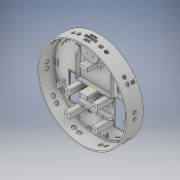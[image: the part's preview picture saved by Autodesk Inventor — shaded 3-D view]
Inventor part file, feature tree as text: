
AUTODESK INVENTOR PART (.ipt)
format: ipt  version: 2018 (Build 220112000, 112)  size: 3,257,856 bytes
history: native  units: in
note: dims shown in document units (in); Inventor stores cm internally (conversion verified against a paired STEP export)
features: extrude x34, fillet x14, sketch x12, chamfer x9, plane x3, emboss x3, pattern_circular x1
ambient origin geometry x8: Origin, YZ Plane, XZ Plane, XY Plane, X Axis, Y Axis, Z Axis, Center Point
bodies: Solid1 (feature_tree)
feature tree (76):
  sketch  "Sketch1"  dims[d0=15.748in d1=13.7795in]
  extrude  "Extrusion1"  Depth=13.7795in
  extrude  "Extrusion3"  Depth=1.9685in
  extrude  "Extrusion4"  Depth=1.9685in
  extrude  "Extrusion5"  Depth=7.874in
  extrude  "Extrusion6"  Depth=1.6811in
  extrude  "Extrusion8"  Depth=1.5748in
  extrude  "Extrusion9"  Depth=2.2835in
  chamfer  "Chamfer1"  Distance=0.4724in
  fillet  "Fillet2"  Radius=0.4724in
  fillet  "Fillet3"  Radius=2.0472in
  fillet  "Fillet4"  Radius=2.2638in
  extrude  "Extrusion12"  Depth=0.3937in
  extrude  "Extrusion15"  Depth=0.3937in
  extrude  "Extrusion16"  Depth=0.3937in
  extrude  "Extrusion17"  Depth=0.3937in
  chamfer  "Chamfer9"  Distance=0.7087in
  extrude  "Extrusion18"  Depth=0.3937in
  extrude  "Extrusion19"  Depth=0.3937in
  plane  "Work Plane1"
  extrude  "Extrusion20"  Depth=0.3937in
  fillet  "Fillet8"  Radius=1.9685in
  pattern_circular  "Circular Pattern1"  [2 undecoded]
  extrude  "Extrusion21"  Depth=0.3937in
  fillet  "Fillet9"  Radius=1.9685in
  sketch  "Sketch6"  dims[d12=3.7795in d13=1.6811in]
  sketch  "Sketch7"  dims[d14=2.3622in d15=1.5748in]
  sketch  "Sketch8"  dims[d16=1.5748in d27=2.2835in]
  extrude  "Extrusion22"  Depth=0.3937in
  extrude  "Extrusion23"  Depth=0.3937in
  extrude  "Extrusion24"  Depth=0.3937in
  extrude  "Extrusion25"  Depth=0.3937in
  fillet  "Fillet12"  Radius=0.3937in
  fillet  "Fillet14"  Radius=0.1181in
  extrude  "Extrusion26"  Depth=0.3937in
  extrude  "Extrusion27"  Depth=0.3937in
  extrude  "Extrusion28"  Depth=0.3937in
  extrude  "Extrusion29"  Depth=0.3937in
  extrude  "Extrusion30"  Depth=0.3937in
  extrude  "Extrusion31"  Depth=0.3937in
  extrude  "Extrusion32"  Depth=0.3937in
  extrude  "Extrusion33"  Depth=0.3937in
  extrude  "Extrusion34"  Depth=0.3937in
  extrude  "Extrusion35"  Depth=0.3937in
  emboss  "Emboss4"
  extrude  "Extrusion36"  Depth=0.3937in
  fillet  "Fillet15"  Radius=0.7087in
  chamfer  "Chamfer10"  Distance=1.0748in
  chamfer  "Chamfer11"  Distance=1.0748in
  chamfer  "Chamfer12"  Distance=0.1969in
  fillet  "Fillet17"  Radius=0.1969in
  fillet  "Fillet18"  Radius=0.1969in
  chamfer  "Chamfer13"  Distance=0.1969in
  chamfer  "Chamfer14"  Distance=0.2362in
  extrude  "Extrusion37"  Depth=0.3937in
  fillet  "Fillet19"  Radius=0.1575in
  fillet  "Fillet20"  Radius=0.2362in
  fillet  "Fillet21"  Radius=0.1575in
  sketch  "Sketch12"  dims[d29=4.3307in]
  extrude  "Extrusion38"  Depth=0.3937in TaperAngle=360.0deg
  extrude  "Extrusion39"  Depth=0.3937in TaperAngle=0.0deg
  fillet  "Fillet22"  Radius=0.8268in
  chamfer  "Chamfer16"  Distance=0.1181in
  chamfer  "Chamfer17"  Distance=0.1181in
  plane  "Work Plane3"
  sketch  "Sketch14"  dims[d31=2.6181in]
  extrude  "Extrusion40"  Depth=0.3937in TaperAngle=0.0deg
  plane  "Work Plane4"
  emboss  "Emboss6"
  emboss  "Emboss7"
  sketch  "Sketch3"  dims[d3=15.3543in d4=1.9685in]
  sketch  "Sketch4"  dims[d5=4.4882in d7=1.9685in]
  sketch  "Sketch5"  dims[d10=7.874in d11=3.7795in]
  sketch  "Sketch9"  dims[d28=4.3307in]
  sketch  "Sketch13"  dims[d30=1.437in]
  sketch  "Sketch15"  dims[d32=1.6811in d33=0.4724in d34=0.4724in d35=2.0472in d48=2.2638in d49=4.4882in d50=0.5906in d51=0.1181in d52=0.1181in d53=0.7087in d54=0.5906in d55=0.1181in d56=0.7087in d57=1.9685in d58=0.3937in d59=0.7874in d60=1.9685in d61=0.3937in d62=0.7874in d63=0.3937in d64=0.1181in d65=0.3937in d66=0.1181in d67=0.1181in d68=0.7087in d69=0.1181in d70=0.5906in d71=0.3937in d72=0.1181in d73=0.1181in d74=0.7087in d75=0.3937in d76=0.1181in d77=0.1181in d78=0.7087in d79=1.0748in d80=1.0748in d81=0.1969in d82=0.1969in d83=0.1969in d84=0.1969in d86=0.2362in d87=0.4724in d88=0.1575in d89=0.2362in d90=0.1575in d91=4.7244in d93=360.0deg d95=2.7559in d96=0.0in d99=0.8268in d100=0.1969in d101=0.0in d102=0.0in d103=0.1181in d104=0.1181in d105=0.1181in d106=0.0in d107=0.1969in d108=0.0in d109=0.1181in d110=0.1969in d111=0.0in d112=0.0in d113=0.1181in d114=0.0in d119=0.1181in d120=0.1969in d121=0.0in d122=0.0in d123=1.1811in d124=0.1969in d125=0.0in d126=0.0in d131=0.3937in d132=0.0787in d133=45.0deg d135=0.0787in d136=0.0787in d137=0.0394in d150=3.1496in d151=0.1969in d154=1.2244in d155=0.0in d163=1.8504in d164=5.9843in d165=3.7402in d166=0.1969in d167=0.1969in d168=0.1969in d169=1.1811in d170=2.3622in d171=0.6693in d172=0.7874in d173=0.0in d183=1.0236in d184=0.5118in d185=0.5118in d186=0.1969in d187=0.1969in d188=1.0236in d189=0.5118in d190=1.0236in d191=0.1969in d192=0.1969in d193=0.1969in d194=0.1969in d195=0.1969in d196=0.1969in d197=1.9685in d198=0.0in d199=0.7874in d200=1.5748in d201=0.7874in d202=1.5748in d203=0.5906in d204=2.5984in d205=0.0in d206=0.0787in d207=0.7874in d208=45.0deg d209=0.2953in d210=0.3937in d211=0.7874in d212=0.1969in d213=0.1969in d214=1.1811in d215=0.0in d216=0.3937in d217=0.7874in d218=0.1969in d219=0.1969in d220=1.1811in d221=0.0in d222=1.378in d223=0.5118in d224=1.0236in d225=0.6339in d226=0.6339in d227=0.4724in d228=0.0in d229=0.0394in d230=3.937in d231=360.0deg d233=4.7244in d234=0.9843in d235=0.9843in d236=0.9843in d237=0.9843in d238=0.9843in d239=0.9843in d240=0.9843in d242=2.9528in d243=0.0in d244=0.1181in d245=0.4921in d246=0.4724in d247=0.4921in d248=0.4724in d249=0.4921in d250=0.4724in d251=0.4921in d252=0.4724in d253=1.5748in d254=0.0in d255=1.5748in d256=0.0in d257=1.5748in d258=0.0in d259=0.4921in d260=0.4724in d261=1.5748in d262=0.0in d271=0.0787in d273=0.0394in d276=2.2323in d277=0.5906in d278=0.1181in d279=0.5906in d280=0.1181in d281=0.1181in d282=0.7087in d283=0.5906in d284=0.7087in d285=0.1181in d286=0.5906in d287=0.1181in d289=0.1969in d290=0.0in d291=0.1969in d292=0.0in d293=0.1969in d294=0.0in d295=0.1969in d296=0.0in d297=0.1969in d298=0.0in d299=0.1969in d300=0.0in d301=0.1969in d302=0.0in d303=0.1969in d304=0.0in d305=0.1969in d306=0.0in d307=0.1181in d308=0.1969in d309=0.0in d310=0.0in d311=0.0787in d312=0.0in d315=0.1969in d316=0.0in d317=0.0394in d318=0.7874in d319=0.3937in d320=45.0deg d321=0.7874in d322=0.3937in d323=45.0deg d324=0.3937in d325=0.3937in d326=45.0deg d328=0.1181in d329=0.1181in d330=0.7874in d331=0.3937in d332=45.0deg d333=0.7874in d334=0.3937in d335=45.0deg d336=0.7874in d337=0.0in d338=0.0394in d339=0.0394in d340=0.0394in d341=8.2677in d342=0.1969in d343=0.0in d344=1.9685in d345=0.0in d346=0.1969in d350=0.7874in d351=0.3937in d352=45.0deg d353=0.7874in d354=0.3937in d355=45.0deg d356=0.7874in d357=0.5118in d358=0.3937in d359=0.3937in d360=0.0in d361=0.0787in d362=0.0in d363=0.0394in d364=0.0in]
note: 2 required parameter values undecoded (feature->parameter linkage not recoverable at this tier; creation-order binding heuristic only, values carry confidence <= 0.55)
